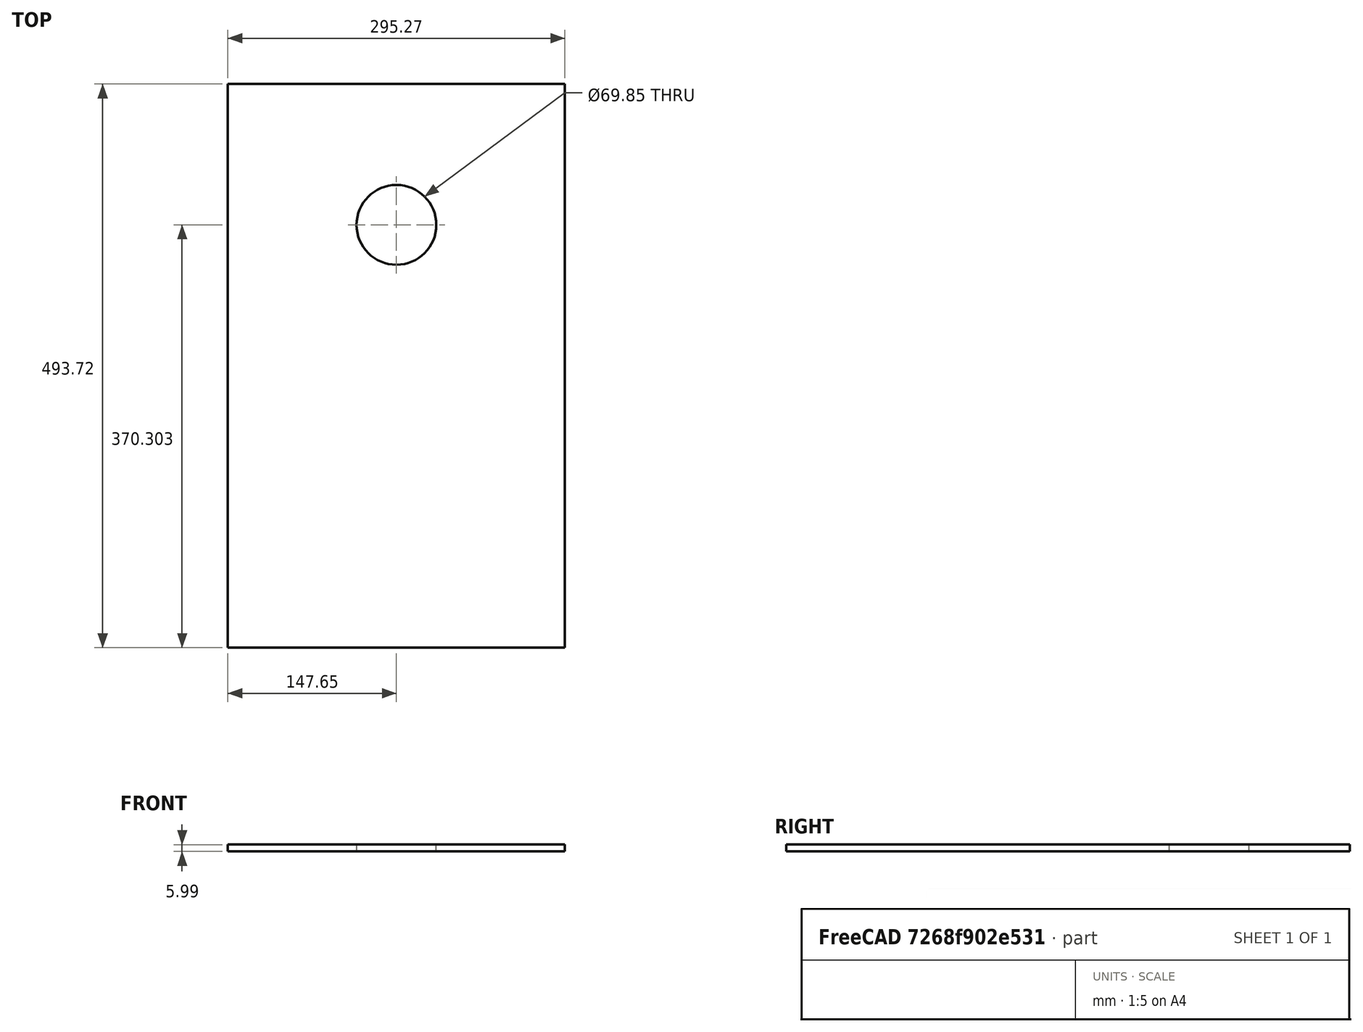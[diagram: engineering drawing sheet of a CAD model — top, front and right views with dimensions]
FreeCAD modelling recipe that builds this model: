
FCSTD DOCUMENT  (FreeCAD 0.19R24267 (Git))
Label: Up1-P4
License: All rights reserved
LicenseURL: http://en.wikipedia.org/wiki/All_rights_reserved
objects: TechDraw::DrawViewDimension×6, TechDraw::DrawProjGroupItem×2, TechDraw::DrawHatch×2, TechDraw::DrawViewAnnotation×2, Sketcher::SketchObject×1, Part::Extrusion×1, TechDraw::DrawSVGTemplate×1, TechDraw::DrawProjGroup×1, TechDraw::DrawPage×1
note: 2 computed .brp shape members not serialized (recipe doc carries the construction recipe); baked Part::Feature solids carry a one-line shape summary decoded from their .brp

FEATURE [Sketcher::SketchObject] Sketch
  FullyConstrained = false
  sketch-geometry (5):
    g0: LineSegment StartX=-122.301 StartY=163.542 StartZ=0 EndX=172.974 EndY=163.542 EndZ=0
    g1: LineSegment StartX=172.974 StartY=163.542 StartZ=0 EndX=172.974 EndY=-330.184 EndZ=0
    g2: LineSegment StartX=172.974 StartY=-330.184 StartZ=0 EndX=-122.301 EndY=-330.184 EndZ=0
    g3: LineSegment StartX=-122.301 StartY=-330.184 StartZ=0 EndX=-122.301 EndY=163.542 EndZ=0
    g4: Circle CenterX=25.3497 CenterY=40.1229 CenterZ=0 NormalX=0 NormalY=0 NormalZ=1 AngleXU=0 Radius=34.925
  constraints (13):
    c: Coincident(g0,g1)
    c: Coincident(g1,g2)
    c: Coincident(g2,g3)
    c: Coincident(g3,g0)
    c: Horizontal(g0)
    c: Horizontal(g2)
    c: Vertical(g1)
    c: Vertical(g3)
    c: Distance(g0,g2) = 493.725
    c: Distance(g0,g1) = 295.275
    c: Diameter(g4) = 69.85
    c: Distance(g4,g0) = 123.419
    c: Distance(g4,g3) = 147.65
FEATURE [Part::Extrusion] Extrude
  Base = -> Sketch
  Dir = (0,0,1)
  DirMode = 2
  FaceMakerClass = Part::FaceMakerBullseye
  LengthFwd = 5.9944
  LengthRev = 0
  Solid = true
  Symmetric = false
FEATURE [TechDraw::DrawSVGTemplate] Template
  Height = 215.9
  Orientation = 1
  Width = 279.4
FEATURE [TechDraw::DrawProjGroupItem] ProjItem  label="Front"
  CoarseView = false
  Direction = (0,0,-1)
  Focus = 100
  HardHidden = false
  IsoCount = 0
  IsoHidden = false
  IsoVisible = false
  LockPosition = true
  Perspective = false
  Rotation = 0
  RotationVector = (-1,0,0)
  Scale = 0.25
  ScaleType = 2
  SeamHidden = false
  SeamVisible = true
  SmoothHidden = false
  SmoothVisible = true
  Source = -> [Extrude]
  Type = 0
  X = 0
  XDirection = (-1,0,0)
  Y = 0
FEATURE [TechDraw::DrawProjGroupItem] ProjItem001  label="Left"
  CoarseView = false
  Direction = (1,0,-1e-16)
  Focus = 100
  HardHidden = false
  IsoCount = 0
  IsoHidden = false
  IsoVisible = false
  LockPosition = false
  Perspective = false
  Rotation = 0
  RotationVector = (1,0,0)
  ScaleType = 2
  SeamHidden = false
  SeamVisible = true
  SmoothHidden = false
  SmoothVisible = true
  Source = -> [Extrude]
  Type = 1
  X = 68.4428
  XDirection = (-1e-16,0,-1)
  Y = 0
FEATURE [TechDraw::DrawProjGroup] ProjGroup
  Anchor = -> ProjItem
  AutoDistribute = true
  LockPosition = false
  ProjectionType = 0
  Rotation = 0
  Scale = 0.25
  ScaleType = 2
  Source = -> [Extrude]
  Views = -> [ProjItem,ProjItem001]
  X = 139.7
  Y = 107.95
  spacingX = 15.0114
  spacingY = 15.0114
FEATURE [TechDraw::DrawViewDimension] Dimension
  Arbitrary = false
  ArbitraryTolerances = false
  EqualTolerance = true
  FormatSpec = %.3f
  FormatSpecOverTolerance = %+.3f
  FormatSpecUnderTolerance = %+.3f
  Inverted = false
  LockPosition = false
  MeasureType = 1
  OverTolerance = 0
  References2D = -> [ProjItem]
  Rotation = 0
  ScaleType = 0
  TheoreticalExact = false
  Type = 2
  UnderTolerance = 0
  X = 48.8262
  Y = 0.441363
FEATURE [TechDraw::DrawViewDimension] Dimension001
  Arbitrary = false
  ArbitraryTolerances = false
  EqualTolerance = true
  FormatSpec = %.3f
  FormatSpecOverTolerance = %+.3f
  FormatSpecUnderTolerance = %+.3f
  Inverted = false
  LockPosition = false
  MeasureType = 1
  OverTolerance = 0
  References2D = -> [ProjItem001]
  Rotation = 0
  ScaleType = 0
  TheoreticalExact = false
  Type = 1
  UnderTolerance = 0
  X = 15.1799
  Y = 46.9105
FEATURE [TechDraw::DrawViewDimension] Dimension002
  Arbitrary = false
  ArbitraryTolerances = false
  EqualTolerance = true
  FormatSpec = %.3f
  FormatSpecOverTolerance = %+.3f
  FormatSpecUnderTolerance = %+.3f
  Inverted = false
  LockPosition = false
  MeasureType = 1
  OverTolerance = 0
  References2D = -> [ProjItem]
  Rotation = 0
  ScaleType = 0
  TheoreticalExact = false
  Type = 1
  UnderTolerance = 0
  X = -0.766255
  Y = -73.9757
FEATURE [TechDraw::DrawViewDimension] Dimension003
  Arbitrary = false
  ArbitraryTolerances = false
  EqualTolerance = true
  FormatSpec = ⌀%.3f
  FormatSpecOverTolerance = %+.3f
  FormatSpecUnderTolerance = %+.3f
  Inverted = false
  LockPosition = false
  MeasureType = 1
  OverTolerance = 0
  References2D = -> [ProjItem]
  Rotation = 0
  ScaleType = 0
  TheoreticalExact = false
  Type = 5
  UnderTolerance = 0
  X = -14.8999
  Y = 50.4263
FEATURE [TechDraw::DrawViewDimension] Dimension004
  Arbitrary = false
  ArbitraryTolerances = false
  EqualTolerance = true
  FormatSpec = %.3f
  FormatSpecOverTolerance = %+.3f
  FormatSpecUnderTolerance = %+.3f
  Inverted = false
  LockPosition = false
  MeasureType = 1
  OverTolerance = 0
  References2D = -> [ProjItem]
  Rotation = 0
  ScaleType = 0
  TheoreticalExact = false
  Type = 1
  UnderTolerance = 0
  X = -17.0845
  Y = 14.3542
FEATURE [TechDraw::DrawViewDimension] Dimension005
  Arbitrary = false
  ArbitraryTolerances = false
  EqualTolerance = true
  FormatSpec = %.3f
  FormatSpecOverTolerance = %+.3f
  FormatSpecUnderTolerance = %+.3f
  Inverted = false
  LockPosition = false
  MeasureType = 1
  OverTolerance = 0
  References2D = -> [ProjItem]
  Rotation = 0
  ScaleType = 0
  TheoreticalExact = false
  Type = 2
  UnderTolerance = 0
  X = 18.4376
  Y = 48.3123
FEATURE [TechDraw::DrawHatch] Hatch  label="HatchF0"
  HatchPattern = <path>
  Source = -> ProjItem [Face0]
FEATURE [TechDraw::DrawHatch] Hatch001  label="Hatch001F0"
  HatchPattern = <path>
  Source = -> ProjItem001 [Face0]
FEATURE [TechDraw::DrawViewAnnotation] Annotation
  Font = osifont
  LineSpace = 80
  LockPosition = false
  MaxWidth = -1
  Rotation = 0
  ScaleType = 0
  Text = Figure S3 (Upright) | Panel 4 [left side exterior baffle] | Quantity: 1
  TextSize = 5.0038
  TextStyle = 0
  X = 46.0547
  Y = 195.58
FEATURE [TechDraw::DrawViewAnnotation] Annotation002
  Font = osifont
  LineSpace = 80
  LockPosition = false
  MaxWidth = -1
  Rotation = 0
  ScaleType = 0
  Text = Units: Inches
  TextSize = 5.0038
  TextStyle = 0
  X = 259.08
  Y = 5.08
FEATURE [TechDraw::DrawPage] Page
  KeepUpdated = true
  NextBalloonIndex = 1
  ProjectionType = 0
  Template = -> Template
  Views = -> [ProjGroup,Dimension,Dimension001,Dimension002,Dimension003,Dimension004,Dimension005,Annotation,Annotation002]
note: 2 file-system paths scrubbed to <path> (originals preserved in the JSON sidecar)
